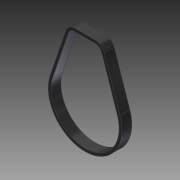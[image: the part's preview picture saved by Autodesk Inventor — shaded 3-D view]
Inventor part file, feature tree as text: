
AUTODESK INVENTOR PART (.ipt)
format: ipt  version: 2014 SP1 (Build 180222100, 222)  size: 96,768 bytes
history: native  units: in
note: dims shown in document units (in); Inventor stores cm internally (conversion verified against a paired STEP export)
features: reference x2, extrude x1, sketch x1
ambient origin geometry x8: Origin, YZ Plane, XZ Plane, XY Plane, X Axis, Y Axis, Z Axis, Center Point
bodies: Solid1 (feature_tree)
feature tree (4):
  extrude  "Extrusion1"  Depth=0.366in TaperAngle=0.0deg
  sketch  "Sketch1"  dims[d0=0.1in d1=0.366in d2=0.0in]
  reference  "Reference2"
  reference  "Reference3"
